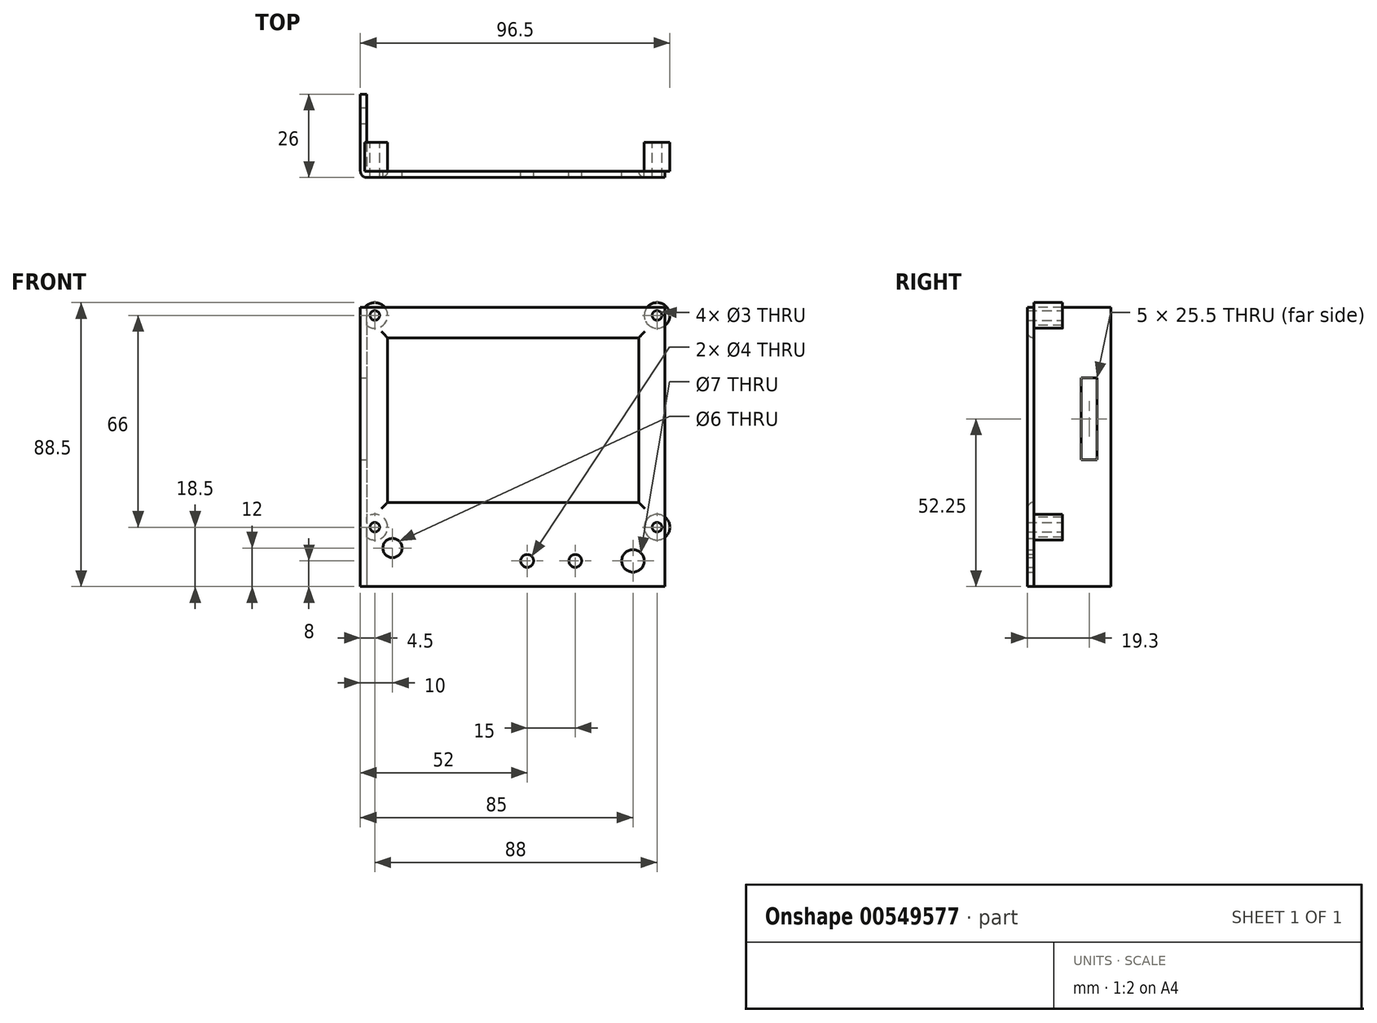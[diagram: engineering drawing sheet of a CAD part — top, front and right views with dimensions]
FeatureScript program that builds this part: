
annotation { "Feature Type Name" : "Feature", "Feature Type Description" : "" }
export const myFeature = defineFeature(function(context is Context, id is Id, definition is map)
    precondition{}
    {
        {
            var Q0;
            Q0=qCreatedBy(makeId("Front.planeOp"),FACE);
            var sketch = newSketch(context, id + "F0", { "sketchPlane" : qUnion([Q0])});
            skLineSegment(sketch, "E0.bottom", {"start": v(-46.5, 43.5) * mm, "end": v(46.5, 43.5) * mm});
            skLineSegment(sketch, "E0.top", {"start": v(-46.5, -43.5) * mm, "end": v(46.5, -43.5) * mm});
            skLineSegment(sketch, "E0.left", {"start": v(-46.5, 43.5) * mm, "end": v(-46.5, -43.5) * mm});
            skLineSegment(sketch, "E0.right", {"start": v(46.5, 43.5) * mm, "end": v(46.5, -43.5) * mm});
            skLineSegment(sketch, "E1.bottom", {"start": v(-40, 34) * mm, "end": v(38.25, 34) * mm});
            skLineSegment(sketch, "E1.top", {"start": v(-40, -17.25) * mm, "end": v(38.25, -17.25) * mm});
            skLineSegment(sketch, "E1.left", {"start": v(-40, 34) * mm, "end": v(-40, -17.25) * mm});
            skLineSegment(sketch, "E1.right", {"start": v(38.25, 34) * mm, "end": v(38.25, -17.25) * mm});
            skCircle(sketch, "E2", {"center": v(36.5, -35.5) * mm, "radius": 3.5 * mm});
            skCircle(sketch, "E3", {"center": v(-38.5, -31.5) * mm, "radius": 3 * mm});
            skCircle(sketch, "E4", {"center": v(18.5, -35.5) * mm, "radius": 2 * mm});
            skCircle(sketch, "E5", {"center": v(3.5, -35.5) * mm, "radius": 2 * mm});
            skLineSegment(sketch, "E6", {"start": v(36.5, -35.5) * mm, "end": v(18.5, -35.5) * mm, "construction": true});
            skLineSegment(sketch, "E7", {"start": v(3.5, -35.5) * mm, "end": v(18.5, -35.5) * mm, "construction": true});
            skSolve(sketch);
        }
        {
            var Q0;
            Q0 = qSketchRegion(id + "F0", true);
            extrude(context, id + "F1", {"entities" : qUnion([Q0]), "depth" : 2 * mm, "offsetDistance" : 25 * mm});
        }
        {
            var Q0;
            Q0=makeQuery(id+"F1.opExtrude","CAP_FACE",FACE,{"disambiguationData":[OSD([sQuery(id+"F0.wireOp",EDGE,"E0.bottom"),sQuery(id+"F0.wireOp",EDGE,"E0.top"),sQuery(id+"F0.wireOp",EDGE,"E0.left"),sQuery(id+"F0.wireOp",EDGE,"E0.right"),sQuery(id+"F0.wireOp",EDGE,"E1.bottom"),sQuery(id+"F0.wireOp",EDGE,"E1.top"),sQuery(id+"F0.wireOp",EDGE,"E1.left"),sQuery(id+"F0.wireOp",EDGE,"E1.right"),sQuery(id+"F0.wireOp",EDGE,"E2"),sQuery(id+"F0.wireOp",EDGE,"E3"),sQuery(id+"F0.wireOp",EDGE,"E4"),sQuery(id+"F0.wireOp",EDGE,"E5")])],"isStart":true});
            var sketch = newSketch(context, id + "F2", { "sketchPlane" : qUnion([Q0])});
            skLineSegment(sketch, "E8.bottom", {"start": v(-44, 41) * mm, "end": v(44, 41) * mm, "construction": true});
            skLineSegment(sketch, "E8.top", {"start": v(-44, -25) * mm, "end": v(44, -25) * mm, "construction": true});
            skLineSegment(sketch, "E8.left", {"start": v(-44, 41) * mm, "end": v(-44, -25) * mm, "construction": true});
            skLineSegment(sketch, "E8.right", {"start": v(44, 41) * mm, "end": v(44, -25) * mm, "construction": true});
            skCircle(sketch, "E9", {"center": v(-44, 41) * mm, "radius": 4 * mm});
            skCircle(sketch, "E10", {"center": v(44, 41) * mm, "radius": 4 * mm});
            skCircle(sketch, "E11", {"center": v(44, -25) * mm, "radius": 4 * mm});
            skCircle(sketch, "E12", {"center": v(-44, -25) * mm, "radius": 4 * mm});
            skSolve(sketch);
        }
        {
            var Q0;
            Q0 = qSketchRegion(id + "F2", true);
            extrude(context, id + "F3", {"entities" : qUnion([Q0]), "operationType" : NewBodyOperationType.ADD, "depth" : 9 * mm, "offsetDistance" : 25 * mm});
        }
        {
            var Q0;
            Q0=makeQuery(id+"F3.opExtrude","CAP_FACE",FACE,{"disambiguationData":[OSD([sQuery(id+"F2.wireOp",EDGE,"E9")])],"isStart":false});
            var sketch = newSketch(context, id + "F4", { "sketchPlane" : qUnion([Q0])});
            skCircle(sketch, "E13", {"center": v(-44, 41) * mm, "radius": 1.5 * mm});
            skCircle(sketch, "E14", {"center": v(44, 41) * mm, "radius": 1.5 * mm});
            skCircle(sketch, "E15", {"center": v(44, -25) * mm, "radius": 1.5 * mm});
            skCircle(sketch, "E16", {"center": v(-44, -25) * mm, "radius": 1.5 * mm});
            skCircle(sketch, "E17.0", {"center": v(44, 41) * mm, "radius": 4 * mm, "construction": true});
            skCircle(sketch, "E18.0", {"center": v(44, -25) * mm, "radius": 4 * mm, "construction": true});
            skCircle(sketch, "E19.0", {"center": v(-44, -25) * mm, "radius": 4 * mm, "construction": true});
            skCircle(sketch, "E20.0", {"center": v(-44, 41) * mm, "radius": 4 * mm, "construction": true});
            skSolve(sketch);
        }
        {
            var Q0;
            Q0 = qSketchRegion(id + "F4", true);
            extrude(context, id + "F5", {"entities" : qUnion([Q0]), "operationType" : NewBodyOperationType.REMOVE, "oppositeDirection" : true, "depth" : 25 * mm, "offsetDistance" : 25 * mm});
        }
        {
            var Q0;
            Q0=makeQuery(id+"F1.opExtrude","SWEPT_FACE",FACE,{"disambiguationData":[OSD([sQuery(id+"F0.wireOp",EDGE,"E0.left")])]});
            var sketch = newSketch(context, id + "F6", { "sketchPlane" : qUnion([Q0])});
            skLineSegment(sketch, "E21.bottom", {"start": v(2, 43.5) * mm, "end": v(-24, 43.5) * mm});
            skLineSegment(sketch, "E21.top", {"start": v(2, -43.5) * mm, "end": v(-24, -43.5) * mm});
            skLineSegment(sketch, "E21.left", {"start": v(2, 43.5) * mm, "end": v(2, -43.5) * mm});
            skLineSegment(sketch, "E21.right", {"start": v(-24, 43.5) * mm, "end": v(-24, -43.5) * mm});
            skLineSegment(sketch, "E22.bottom", {"start": v(-19.8, 21.5) * mm, "end": v(-14.8, 21.5) * mm});
            skLineSegment(sketch, "E22.top", {"start": v(-19.8, -4) * mm, "end": v(-14.8, -4) * mm});
            skLineSegment(sketch, "E22.left", {"start": v(-19.8, 21.5) * mm, "end": v(-19.8, -4) * mm});
            skLineSegment(sketch, "E22.right", {"start": v(-14.8, 21.5) * mm, "end": v(-14.8, -4) * mm});
            skSolve(sketch);
        }
        {
            var Q0;
            Q0 = qSketchRegion(id + "F6", true);
            extrude(context, id + "F7", {"entities" : qUnion([Q0]), "operationType" : NewBodyOperationType.ADD, "depth" : 2 * mm, "offsetDistance" : 25 * mm});
        }
        {
            var Q0;
            Q0=makeQuery(id+"F9.opExtrude","CAP_EDGE",EDGE,{"disambiguationData":[OSD([sQuery(id+"Fwa9TyqcvU6WHnK_1.wireOp",EDGE,"TkvlWiRJ-K5s0-XalZ-jszq-rEh62O2KhFcj.bottom")])],"isStart":false});
            var Q1;
            Q1=makeQuery(id+"F10.opExtrude","CAP_EDGE",EDGE,{"disambiguationData":[OSD([sQuery(id+"FIvMUTywS24l0xW_1.wireOp",EDGE,"htxHLYS5-JyhU-L9ED-BAgq-8vLsVtjvZpRC.right")])],"isStart":false});
            var Q2;
            Q2=makeQuery(id+"F10.opExtrude","CAP_EDGE",EDGE,{"disambiguationData":[OSD([sQuery(id+"FIvMUTywS24l0xW_1.wireOp",EDGE,"htxHLYS5-JyhU-L9ED-BAgq-8vLsVtjvZpRC.left")])],"isStart":false});
            var Q3;
            Q3=makeQuery(id+"F8.opExtrude","CAP_EDGE",EDGE,{"disambiguationData":[OSD([sQuery(id+"F7eiTBmJp871ISI_1.wireOp",EDGE,"BecS1ZPg-B1BR-HTf8-Unsb-VFhvOYgCJDVx.left")])],"isStart":false});
            var Q4;
            Q4=makeQuery(id+"F9.boolean.opBoolean","MERGE",EDGE,{"derivedFrom":[makeQuery(id+"F8.opExtrude","CAP_EDGE",EDGE,{"disambiguationData":[OSD([sQuery(id+"F7eiTBmJp871ISI_1.wireOp",EDGE,"BecS1ZPg-B1BR-HTf8-Unsb-VFhvOYgCJDVx.bottom")])],"isStart":false}),makeQuery(id+"F9.opExtrude","SWEPT_EDGE",EDGE,{"disambiguationData":[OSD([sQuery(id+"Fwa9TyqcvU6WHnK_1.wireOp",EDGE,"TkvlWiRJ-K5s0-XalZ-jszq-rEh62O2KhFcj.bottom"),sQuery(id+"Fwa9TyqcvU6WHnK_1.wireOp",EDGE,"TkvlWiRJ-K5s0-XalZ-jszq-rEh62O2KhFcj.left")])]})]});
            var Q5;
            Q5=makeQuery(id+"F10.boolean.opBoolean","MERGE",EDGE,{"derivedFrom":[makeQuery(id+"F8.boolean.opBoolean","MERGE",EDGE,{"derivedFrom":[makeQuery(id+"F7.opExtrude","CAP_EDGE",EDGE,{"disambiguationData":[OSD([sQuery(id+"F6.wireOp",EDGE,"E21.left")])],"isStart":false}),makeQuery(id+"F8.opExtrude","SWEPT_EDGE",EDGE,{"disambiguationData":[OSD([sQuery(id+"F7eiTBmJp871ISI_1.wireOp",EDGE,"BecS1ZPg-B1BR-HTf8-Unsb-VFhvOYgCJDVx.bottom"),sQuery(id+"F7eiTBmJp871ISI_1.wireOp",EDGE,"BecS1ZPg-B1BR-HTf8-Unsb-VFhvOYgCJDVx.left")])]})]}),makeQuery(id+"F10.opExtrude","SWEPT_EDGE",EDGE,{"disambiguationData":[OSD([sQuery(id+"FIvMUTywS24l0xW_1.wireOp",EDGE,"htxHLYS5-JyhU-L9ED-BAgq-8vLsVtjvZpRC.bottom"),sQuery(id+"FIvMUTywS24l0xW_1.wireOp",EDGE,"htxHLYS5-JyhU-L9ED-BAgq-8vLsVtjvZpRC.left")])]})]});
            var Q6;
            Q6=makeQuery(id+"F10.opExtrude","CAP_EDGE",EDGE,{"disambiguationData":[OSD([sQuery(id+"FIvMUTywS24l0xW_1.wireOp",EDGE,"htxHLYS5-JyhU-L9ED-BAgq-8vLsVtjvZpRC.bottom")])],"isStart":false});
            var Q7;
            Q7=makeQuery(id+"F10.boolean.opBoolean","MERGE",EDGE,{"derivedFrom":[makeQuery(id+"F9.opExtrude","CAP_EDGE",EDGE,{"disambiguationData":[OSD([sQuery(id+"Fwa9TyqcvU6WHnK_1.wireOp",EDGE,"TkvlWiRJ-K5s0-XalZ-jszq-rEh62O2KhFcj.left")])],"isStart":false}),makeQuery(id+"F10.opExtrude","SWEPT_EDGE",EDGE,{"disambiguationData":[OSD([sQuery(id+"FIvMUTywS24l0xW_1.wireOp",EDGE,"htxHLYS5-JyhU-L9ED-BAgq-8vLsVtjvZpRC.bottom"),sQuery(id+"FIvMUTywS24l0xW_1.wireOp",EDGE,"htxHLYS5-JyhU-L9ED-BAgq-8vLsVtjvZpRC.right")])]})]});
            var Q8;
            Q8=makeQuery(id+"F1.opExtrude","CAP_EDGE",EDGE,{"disambiguationData":[OSD([sQuery(id+"F0.wireOp",EDGE,"E1.left")])],"isStart":false});
            var Q9;
            Q9=makeQuery(id+"F11.opExtrude","CAP_EDGE",EDGE,{"disambiguationData":[OSD([sQuery(id+"FIAZ7MrsgKPwHPc_1.wireOp",EDGE,"DIkQMztP-26XJ-0dXI-2aa7-jHDBvHfhHZhQ.right")])],"isStart":false});
            var Q10;
            Q10=makeQuery(id+"F11.opExtrude","CAP_EDGE",EDGE,{"disambiguationData":[OSD([sQuery(id+"FIAZ7MrsgKPwHPc_1.wireOp",EDGE,"DIkQMztP-26XJ-0dXI-2aa7-jHDBvHfhHZhQ.bottom")])],"isStart":false});
            var Q11;
            Q11=makeQuery(id+"F1.opExtrude","CAP_EDGE",EDGE,{"disambiguationData":[OSD([sQuery(id+"F0.wireOp",EDGE,"E1.bottom")])],"isStart":false});
            var Q12;
            Q12=makeQuery(id+"F11.opExtrude","CAP_EDGE",EDGE,{"disambiguationData":[OSD([sQuery(id+"FIAZ7MrsgKPwHPc_1.wireOp",EDGE,"DIkQMztP-26XJ-0dXI-2aa7-jHDBvHfhHZhQ.left")])],"isStart":false});
            var Q13;
            Q13=makeQuery(id+"F1.opExtrude","CAP_EDGE",EDGE,{"disambiguationData":[OSD([sQuery(id+"F0.wireOp",EDGE,"E1.right")])],"isStart":false});
            var Q14;
            Q14=makeQuery(id+"F1.opExtrude","CAP_EDGE",EDGE,{"disambiguationData":[OSD([sQuery(id+"F0.wireOp",EDGE,"E1.top")])],"isStart":false});
            var Q15;
            Q15=makeQuery(id+"F11.opExtrude","CAP_EDGE",EDGE,{"disambiguationData":[OSD([sQuery(id+"FIAZ7MrsgKPwHPc_1.wireOp",EDGE,"DIkQMztP-26XJ-0dXI-2aa7-jHDBvHfhHZhQ.top")])],"isStart":false});
            fillet(context, id + "F12", {"entities" : qUnion([Q0, Q1, Q2, Q3, Q4, Q5, Q6, Q7, Q8, Q9, Q10, Q11, Q12, Q13, Q14, Q15]), "radius" : 2 * mm, "tangentPropagation" : true, "allowEdgeOverflow" : false});
        }
    });
